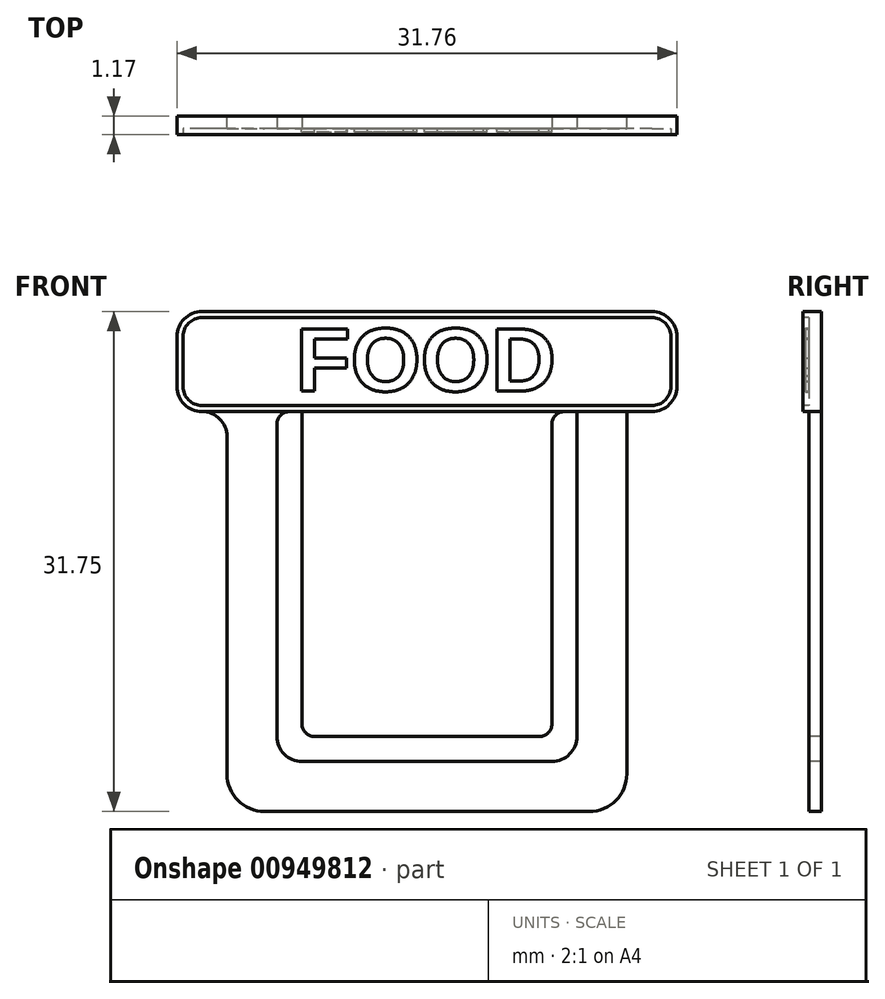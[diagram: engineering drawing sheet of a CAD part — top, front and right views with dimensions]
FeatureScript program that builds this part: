
annotation { "Feature Type Name" : "Feature", "Feature Type Description" : "" }
export const myFeature = defineFeature(function(context is Context, id is Id, definition is map)
    precondition{}
    {
        {
            var Q0;
            Q0=qCreatedBy(makeId("Front.planeOp"),FACE);
            var sketch = newSketch(context, id + "F0", { "sketchPlane" : qUnion([Q0])});
            skLineSegment(sketch, "E0.bottom", {"start": v(12.7, 12.7) * mm, "end": v(-12.7, 12.7) * mm});
            skLineSegment(sketch, "E0.top", {"start": v(12.7, -12.7) * mm, "end": v(-12.7, -12.7) * mm});
            skLineSegment(sketch, "E0.left", {"start": v(12.7, 12.7) * mm, "end": v(12.7, -12.7) * mm});
            skLineSegment(sketch, "E0.right", {"start": v(-12.7, 12.7) * mm, "end": v(-12.7, -12.7) * mm});
            skPoint(sketch, "E0.middle", {"position": v(0, 0) * mm});
            skSolve(sketch);
        }
        {
            var Q0;
            Q0=makeQuery(id+"F0.imprint","IMPRINT",FACE,{"disambiguationData":[TD([[makeQuery(id+"F0.imprint","IMPRINT",EDGE,{"derivedFrom":sQuery(id+"F0.wireOp",EDGE,"E0.bottom")}),1.0]])]});
            extrude(context, id + "F1", {"entities" : qUnion([Q0]), "depth" : 0.8 * mm, "offsetDistance" : 25.4 * mm});
        }
        {
            var Q0;
            Q0=makeQuery(id+"F1.opExtrude","SWEPT_EDGE",EDGE,{"disambiguationData":[OSD([sQuery(id+"F0.wireOp",EDGE,"E0.top"),sQuery(id+"F0.wireOp",EDGE,"E0.left")])]});
            var Q1;
            Q1=makeQuery(id+"F1.opExtrude","SWEPT_EDGE",EDGE,{"disambiguationData":[OSD([sQuery(id+"F0.wireOp",EDGE,"E0.top"),sQuery(id+"F0.wireOp",EDGE,"E0.right")])]});
            fillet(context, id + "F2", {"entities" : qUnion([Q0, Q1]), "radius" : 2.38 * mm, "tangentPropagation" : true, "allowEdgeOverflow" : false});
        }
        {
            var Q0;
            Q0=makeQuery(id+"F1.opExtrude","CAP_FACE",FACE,{"disambiguationData":[OSD([sQuery(id+"F0.wireOp",EDGE,"E0.bottom"),sQuery(id+"F0.wireOp",EDGE,"E0.top"),sQuery(id+"F0.wireOp",EDGE,"E0.left"),sQuery(id+"F0.wireOp",EDGE,"E0.right")])],"isStart":false});
            var sketch = newSketch(context, id + "F3", { "sketchPlane" : qUnion([Q0])});
            skLineSegment(sketch, "E1.bottom", {"start": v(9.52, 12.7) * mm, "end": v(-9.53, 12.7) * mm});
            skLineSegment(sketch, "E1.top", {"start": v(9.53, -9.53) * mm, "end": v(-9.52, -9.53) * mm});
            skLineSegment(sketch, "E1.left", {"start": v(9.52, 12.7) * mm, "end": v(9.53, -9.53) * mm});
            skLineSegment(sketch, "E1.right", {"start": v(-9.53, 12.7) * mm, "end": v(-9.52, -9.53) * mm});
            skPoint(sketch, "E1.middle", {"position": v(0, 0) * mm});
            skSolve(sketch);
        }
        {
            var Q0;
            Q0=makeQuery(id+"F3.imprint","IMPRINT",FACE,{"disambiguationData":[TD([[makeQuery(id+"F3.imprint","IMPRINT",EDGE,{"derivedFrom":sQuery(id+"F3.wireOp",EDGE,"E1.bottom")}),1.0]])]});
            extrude(context, id + "F4", {"entities" : qUnion([Q0]), "operationType" : NewBodyOperationType.REMOVE, "oppositeDirection" : true, "depth" : 4.93 * mm, "offsetDistance" : 25.4 * mm});
        }
        {
            var Q0;
            Q0=makeQuery(id+"F1.opExtrude","CAP_FACE",FACE,{"disambiguationData":[OSD([sQuery(id+"F0.wireOp",EDGE,"E0.bottom"),sQuery(id+"F0.wireOp",EDGE,"E0.top"),sQuery(id+"F0.wireOp",EDGE,"E0.left"),sQuery(id+"F0.wireOp",EDGE,"E0.right")])],"isStart":false});
            var sketch = newSketch(context, id + "F5", { "sketchPlane" : qUnion([Q0])});
            skLineSegment(sketch, "E2.bottom", {"start": v(-15.88, 12.7) * mm, "end": v(15.88, 12.7) * mm});
            skLineSegment(sketch, "E2.top", {"start": v(-15.88, 19.05) * mm, "end": v(15.88, 19.05) * mm});
            skLineSegment(sketch, "E2.left", {"start": v(-15.88, 12.7) * mm, "end": v(-15.88, 19.05) * mm});
            skLineSegment(sketch, "E2.right", {"start": v(15.87, 12.7) * mm, "end": v(15.87, 19.05) * mm});
            skSolve(sketch);
        }
        {
            var Q0;
            Q0=makeQuery(id+"F5.imprint","IMPRINT",FACE,{"disambiguationData":[TD([[makeQuery(id+"F5.imprint","IMPRINT",EDGE,{"derivedFrom":sQuery(id+"F5.wireOp",EDGE,"E2.top")}),-1.0]])]});
            extrude(context, id + "F6", {"entities" : qUnion([Q0]), "operationType" : NewBodyOperationType.ADD, "oppositeDirection" : true, "depth" : 0.8 * mm, "offsetDistance" : 25.4 * mm});
        }
        {
            var Q0;
            Q0=makeQuery(id+"F6.opExtrude","SWEPT_EDGE",EDGE,{"disambiguationData":[OSD([sQuery(id+"F5.wireOp",EDGE,"E2.top"),sQuery(id+"F5.wireOp",EDGE,"E2.left")])]});
            var Q1;
            Q1=makeQuery(id+"F6.opExtrude","SWEPT_EDGE",EDGE,{"disambiguationData":[OSD([sQuery(id+"F5.wireOp",EDGE,"E2.top"),sQuery(id+"F5.wireOp",EDGE,"E2.right")])]});
            var Q2;
            Q2=makeQuery(id+"F6.opExtrude","SWEPT_EDGE",EDGE,{"disambiguationData":[OSD([sQuery(id+"F5.wireOp",EDGE,"E2.bottom"),sQuery(id+"F5.wireOp",EDGE,"E2.right")])]});
            var Q3;
            Q3=makeQuery(id+"F1.opExtrude","SWEPT_EDGE",EDGE,{"disambiguationData":[OSD([sQuery(id+"F0.wireOp",EDGE,"E0.bottom"),sQuery(id+"F0.wireOp",EDGE,"E0.left")])]});
            var Q4;
            Q4=makeQuery(id+"F6.opExtrude","SWEPT_EDGE",EDGE,{"disambiguationData":[OSD([sQuery(id+"F5.wireOp",EDGE,"E2.bottom"),sQuery(id+"F5.wireOp",EDGE,"E2.left")])]});
            var Q5;
            Q5=makeQuery(id+"F1.opExtrude","SWEPT_EDGE",EDGE,{"disambiguationData":[OSD([sQuery(id+"F0.wireOp",EDGE,"E0.bottom"),sQuery(id+"F0.wireOp",EDGE,"E0.right")])]});
            fillet(context, id + "F7", {"entities" : qUnion([Q0, Q1, Q2, Q3, Q4, Q5]), "radius" : 1.59 * mm, "tangentPropagation" : true, "allowEdgeOverflow" : false});
        }
        {
            var Q0;
            Q0=makeQuery(id+"F4.boolean.opBoolean","COPY",EDGE,{"derivedFrom":makeQuery(id+"F4.opExtrude","SWEPT_EDGE",EDGE,{"disambiguationData":[OSD([sQuery(id+"F3.wireOp",EDGE,"E1.top"),sQuery(id+"F3.wireOp",EDGE,"E1.right")])]})});
            var Q1;
            Q1=makeQuery(id+"F4.boolean.opBoolean","COPY",EDGE,{"derivedFrom":makeQuery(id+"F4.opExtrude","SWEPT_EDGE",EDGE,{"disambiguationData":[OSD([sQuery(id+"F3.wireOp",EDGE,"E1.top"),sQuery(id+"F3.wireOp",EDGE,"E1.left")])]})});
            fillet(context, id + "F8", {"entities" : qUnion([Q0, Q1]), "radius" : 1.59 * mm, "tangentPropagation" : true, "allowEdgeOverflow" : false});
        }
        {
            var Q0;
            Q0=makeQuery(id+"F6.boolean.opBoolean","MERGE",FACE,{"derivedFrom":[makeQuery(id+"F1.opExtrude","CAP_FACE",FACE,{"disambiguationData":[OSD([sQuery(id+"F0.wireOp",EDGE,"E0.bottom"),sQuery(id+"F0.wireOp",EDGE,"E0.top"),sQuery(id+"F0.wireOp",EDGE,"E0.left"),sQuery(id+"F0.wireOp",EDGE,"E0.right")])],"isStart":false}),makeQuery(id+"F6.opExtrude","CAP_FACE",FACE,{"disambiguationData":[OSD([sQuery(id+"F5.wireOp",EDGE,"E2.bottom"),sQuery(id+"F5.wireOp",EDGE,"E2.top"),sQuery(id+"F5.wireOp",EDGE,"E2.left"),sQuery(id+"F5.wireOp",EDGE,"E2.right")])],"isStart":true})]});
            var sketch = newSketch(context, id + "F9", { "sketchPlane" : qUnion([Q0])});
            skLineSegment(sketch, "E3.bottom", {"start": v(-7.94, 12.7) * mm, "end": v(7.94, 12.7) * mm});
            skLineSegment(sketch, "E3.top", {"start": v(-7.94, -7.94) * mm, "end": v(7.94, -7.94) * mm});
            skLineSegment(sketch, "E3.left", {"start": v(-7.94, 12.7) * mm, "end": v(-7.94, -7.94) * mm});
            skLineSegment(sketch, "E3.right", {"start": v(7.94, 12.7) * mm, "end": v(7.94, -7.94) * mm});
            skSolve(sketch);
        }
        {
            var Q0;
            Q0=makeQuery(id+"F9.imprint","IMPRINT",FACE,{"disambiguationData":[TD([[makeQuery(id+"F9.imprint","IMPRINT",EDGE,{"derivedFrom":sQuery(id+"F9.wireOp",EDGE,"E3.bottom")}),1.0]])]});
            extrude(context, id + "F10", {"entities" : qUnion([Q0]), "operationType" : NewBodyOperationType.ADD, "oppositeDirection" : true, "depth" : 0.8 * mm, "offsetDistance" : 25.4 * mm});
        }
        {
            var Q0;
            Q0=makeQuery(id+"F10.opExtrude","SWEPT_EDGE",EDGE,{"disambiguationData":[OSD([sQuery(id+"F5.wireOp",EDGE,"E2.bottom"),sQuery(id+"F9.wireOp",EDGE,"E3.bottom"),sQuery(id+"F9.wireOp",EDGE,"E3.left")])]});
            var Q1;
            Q1=makeQuery(id+"F4.boolean.opBoolean","COPY",EDGE,{"derivedFrom":makeQuery(id+"F4.opExtrude","SWEPT_EDGE",EDGE,{"disambiguationData":[OSD([sQuery(id+"F0.wireOp",EDGE,"E0.bottom"),sQuery(id+"F3.wireOp",EDGE,"E1.bottom"),sQuery(id+"F3.wireOp",EDGE,"E1.right")])]})});
            var Q2;
            Q2=makeQuery(id+"F10.opExtrude","SWEPT_EDGE",EDGE,{"disambiguationData":[OSD([sQuery(id+"F5.wireOp",EDGE,"E2.bottom"),sQuery(id+"F9.wireOp",EDGE,"E3.bottom"),sQuery(id+"F9.wireOp",EDGE,"E3.right")])]});
            var Q3;
            Q3=makeQuery(id+"F4.boolean.opBoolean","COPY",EDGE,{"derivedFrom":makeQuery(id+"F4.opExtrude","SWEPT_EDGE",EDGE,{"disambiguationData":[OSD([sQuery(id+"F0.wireOp",EDGE,"E0.bottom"),sQuery(id+"F3.wireOp",EDGE,"E1.bottom"),sQuery(id+"F3.wireOp",EDGE,"E1.left")])]})});
            fillet(context, id + "F11", {"entities" : qUnion([Q0, Q1, Q2, Q3]), "radius" : 0.8 * mm, "tangentPropagation" : true, "allowEdgeOverflow" : false});
        }
        {
            var Q0;
            Q0=makeQuery(id+"F10.opExtrude","SWEPT_EDGE",EDGE,{"disambiguationData":[OSD([sQuery(id+"F9.wireOp",EDGE,"E3.top"),sQuery(id+"F9.wireOp",EDGE,"E3.left")])]});
            var Q1;
            Q1=makeQuery(id+"F10.opExtrude","SWEPT_EDGE",EDGE,{"disambiguationData":[OSD([sQuery(id+"F9.wireOp",EDGE,"E3.top"),sQuery(id+"F9.wireOp",EDGE,"E3.right")])]});
            fillet(context, id + "F12", {"entities" : qUnion([Q0, Q1]), "radius" : 0.8 * mm, "tangentPropagation" : true, "allowEdgeOverflow" : false});
        }
        {
            var Q0;
            Q0=makeQuery(id+"F10.boolean.opBoolean","MERGE",FACE,{"derivedFrom":[makeQuery(id+"F6.boolean.opBoolean","MERGE",FACE,{"derivedFrom":[makeQuery(id+"F1.opExtrude","CAP_FACE",FACE,{"disambiguationData":[OSD([sQuery(id+"F0.wireOp",EDGE,"E0.bottom"),sQuery(id+"F0.wireOp",EDGE,"E0.top"),sQuery(id+"F0.wireOp",EDGE,"E0.left"),sQuery(id+"F0.wireOp",EDGE,"E0.right")])],"isStart":false}),makeQuery(id+"F6.opExtrude","CAP_FACE",FACE,{"disambiguationData":[OSD([sQuery(id+"F5.wireOp",EDGE,"E2.bottom"),sQuery(id+"F5.wireOp",EDGE,"E2.top"),sQuery(id+"F5.wireOp",EDGE,"E2.left"),sQuery(id+"F5.wireOp",EDGE,"E2.right")])],"isStart":true})]}),makeQuery(id+"F10.opExtrude","CAP_FACE",FACE,{"disambiguationData":[OSD([sQuery(id+"F9.wireOp",EDGE,"E3.bottom"),sQuery(id+"F9.wireOp",EDGE,"E3.top"),sQuery(id+"F9.wireOp",EDGE,"E3.left"),sQuery(id+"F9.wireOp",EDGE,"E3.right")])],"isStart":true})]});
            var sketch = newSketch(context, id + "F13", { "sketchPlane" : qUnion([Q0])});
            skArc(sketch, "E4.0", {"start": v(-14.29, 19.05) * mm, "mid": v(-15.41, 18.59) * mm, "end": v(-15.88, 17.46) * mm});
            skLineSegment(sketch, "E5.0", {"start": v(-15.88, 14.29) * mm, "end": v(-15.88, 17.46) * mm});
            skArc(sketch, "E6.0", {"start": v(-15.88, 14.29) * mm, "mid": v(-15.41, 13.16) * mm, "end": v(-14.29, 12.7) * mm});
            skLineSegment(sketch, "E7.0", {"start": v(-14.29, 19.05) * mm, "end": v(14.29, 19.05) * mm});
            skArc(sketch, "E8.0", {"start": v(15.87, 17.46) * mm, "mid": v(15.41, 18.59) * mm, "end": v(14.29, 19.05) * mm});
            skLineSegment(sketch, "E9.0", {"start": v(15.87, 14.29) * mm, "end": v(15.87, 17.46) * mm});
            skArc(sketch, "E10.0", {"start": v(14.29, 12.7) * mm, "mid": v(15.41, 13.16) * mm, "end": v(15.87, 14.29) * mm});
            skLineSegment(sketch, "E11", {"start": v(-14.29, 12.7) * mm, "end": v(14.29, 12.7) * mm});
            skSolve(sketch);
        }
        {
            var Q0;
            Q0=makeQuery(id+"F13.imprint","IMPRINT",FACE,{"disambiguationData":[TD([[makeQuery(id+"F13.imprint","IMPRINT",EDGE,{"derivedFrom":sQuery(id+"F13.wireOp",EDGE,"E4.0")}),1.0]])]});
            extrude(context, id + "F14", {"entities" : qUnion([Q0]), "operationType" : NewBodyOperationType.ADD, "depth" : 0.38 * mm, "offsetDistance" : 25.4 * mm});
        }
        {
            var Q0;
            Q0=makeQuery(id+"F14.opExtrude","CAP_FACE",FACE,{"disambiguationData":[OSD([sQuery(id+"F13.wireOp",EDGE,"E4.0"),sQuery(id+"F13.wireOp",EDGE,"E5.0"),sQuery(id+"F13.wireOp",EDGE,"E6.0"),sQuery(id+"F13.wireOp",EDGE,"E7.0"),sQuery(id+"F13.wireOp",EDGE,"E8.0"),sQuery(id+"F13.wireOp",EDGE,"E9.0"),sQuery(id+"F13.wireOp",EDGE,"E10.0"),sQuery(id+"F13.wireOp",EDGE,"E11")])],"isStart":false});
            var sketch = newSketch(context, id + "F15", { "sketchPlane" : qUnion([Q0])});
            skArc(sketch, "E12.0", {"start": v(-14.29, 19.05) * mm, "mid": v(-15.41, 18.59) * mm, "end": v(-15.88, 17.46) * mm});
            skLineSegment(sketch, "E13.0", {"start": v(-14.29, 19.05) * mm, "end": v(14.29, 19.05) * mm});
            skLineSegment(sketch, "E14.0", {"start": v(-15.88, 14.29) * mm, "end": v(-15.88, 17.46) * mm});
            skArc(sketch, "E15.0", {"start": v(-15.88, 14.29) * mm, "mid": v(-15.41, 13.16) * mm, "end": v(-14.29, 12.7) * mm});
            skLineSegment(sketch, "E16.0", {"start": v(-14.29, 12.7) * mm, "end": v(14.29, 12.7) * mm});
            skArc(sketch, "E17.0", {"start": v(14.29, 12.7) * mm, "mid": v(15.41, 13.16) * mm, "end": v(15.87, 14.29) * mm});
            skArc(sketch, "E18.0", {"start": v(15.87, 17.46) * mm, "mid": v(15.41, 18.59) * mm, "end": v(14.29, 19.05) * mm});
            skArc(sketch, "E19", {"start": v(-14.29, 18.67) * mm, "mid": v(-15.14, 18.32) * mm, "end": v(-15.5, 17.46) * mm});
            skArc(sketch, "E20", {"start": v(-15.5, 14.29) * mm, "mid": v(-15.14, 13.43) * mm, "end": v(-14.29, 13.08) * mm});
            skArc(sketch, "E21", {"start": v(15.5, 17.46) * mm, "mid": v(15.14, 18.32) * mm, "end": v(14.29, 18.67) * mm});
            skArc(sketch, "E22", {"start": v(14.29, 13.08) * mm, "mid": v(15.14, 13.43) * mm, "end": v(15.5, 14.29) * mm});
            skLineSegment(sketch, "E23", {"start": v(-14.29, 19.05) * mm, "end": v(-14.29, 12.7) * mm, "construction": true});
            skLineSegment(sketch, "E24", {"start": v(-15.88, 17.46) * mm, "end": v(15.87, 17.46) * mm, "construction": true});
            skLineSegment(sketch, "E25", {"start": v(14.29, 19.05) * mm, "end": v(14.29, 12.7) * mm, "construction": true});
            skLineSegment(sketch, "E26", {"start": v(15.87, 14.29) * mm, "end": v(-15.88, 14.29) * mm, "construction": true});
            skLineSegment(sketch, "E27", {"start": v(14.29, 18.67) * mm, "end": v(-14.29, 18.67) * mm});
            skLineSegment(sketch, "E28", {"start": v(-15.5, 17.46) * mm, "end": v(-15.5, 14.29) * mm});
            skLineSegment(sketch, "E29", {"start": v(-14.29, 13.08) * mm, "end": v(14.29, 13.08) * mm});
            skLineSegment(sketch, "E30", {"start": v(15.5, 17.46) * mm, "end": v(15.5, 14.29) * mm});
            skSolve(sketch);
        }
        {
            var Q0;
            Q0=makeQuery(id+"F15.imprint","IMPRINT",FACE,{"disambiguationData":[TD([[makeQuery(id+"F15.imprint","IMPRINT",EDGE,{"derivedFrom":sQuery(id+"F15.wireOp",EDGE,"E19")}),1.0]])]});
            var Q1;
            {var subQ0=sQuery(id+"F9.wireOp",EDGE,"E3.right");var subQ1=sQuery(id+"F9.wireOp",EDGE,"E3.top");var subQ3=sQuery(id+"F0.wireOp",EDGE,"E0.bottom");var subQ4=sQuery(id+"F9.wireOp",EDGE,"E3.left");var subQ5=makeQuery(id+"F6.opExtrude","CAP_FACE",FACE,{"disambiguationData":[OSD([sQuery(id+"F5.wireOp",EDGE,"E2.bottom"),sQuery(id+"F5.wireOp",EDGE,"E2.top"),sQuery(id+"F5.wireOp",EDGE,"E2.left"),sQuery(id+"F5.wireOp",EDGE,"E2.right")])],"isStart":true});var subQ6=makeQuery(id+"F1.opExtrude","CAP_FACE",FACE,{"disambiguationData":[OSD([subQ3,sQuery(id+"F0.wireOp",EDGE,"E0.top"),sQuery(id+"F0.wireOp",EDGE,"E0.left"),sQuery(id+"F0.wireOp",EDGE,"E0.right")])],"isStart":false});var subQ7=makeQuery(id+"F10.opExtrude","CAP_FACE",FACE,{"disambiguationData":[OSD([sQuery(id+"F9.wireOp",EDGE,"E3.bottom"),subQ1,subQ4,subQ0])],"isStart":true});Q1=makeQuery(id+"F14.boolean.opBoolean","SPLIT",FACE,{"disambiguationData":[TD([makeQuery(id+"F10.opExtrude","SWEPT_FACE",FACE,{"disambiguationData":[OSD([subQ1])]})])],"derivedFrom":makeQuery(id+"F10.boolean.opBoolean","MERGE",FACE,{"derivedFrom":[makeQuery(id+"F6.boolean.opBoolean","MERGE",FACE,{"derivedFrom":[subQ6,subQ5]}),subQ7]})});}
            extrude(context, id + "F16", {"entities" : qUnion([Q0]), "operationType" : NewBodyOperationType.REMOVE, "endBound" : BoundingType.UP_TO_SURFACE, "oppositeDirection" : true, "depth" : 25.4 * mm, "endBoundEntityFace" : qUnion([Q1]), "offsetDistance" : 25.4 * mm});
        }
        {
            var Q0;
            Q0=qCreatedBy(makeId("Front.planeOp"),FACE);
            var sketch = newSketch(context, id + "F17", { "sketchPlane" : qUnion([Q0])});
            skText(sketch, "E31", { "text": "FOOD", "fontName": "Arimo-Bold.ttf"});
            const initialGuessF17  = {"E31": [-0.00834, 0.01401, 1, 0, 0.00412]};
            skSetInitialGuess(sketch, initialGuessF17);
            skSolve(sketch);
        }
        {
            var Q0;
            Q0=qSketchRegion(id+"F17",true);
            extrude(context, id + "F18", {"entities" : qUnion([Q0]), "operationType" : NewBodyOperationType.ADD, "depth" : 1.02 * mm, "offsetDistance" : 25.4 * mm});
        }
    });
